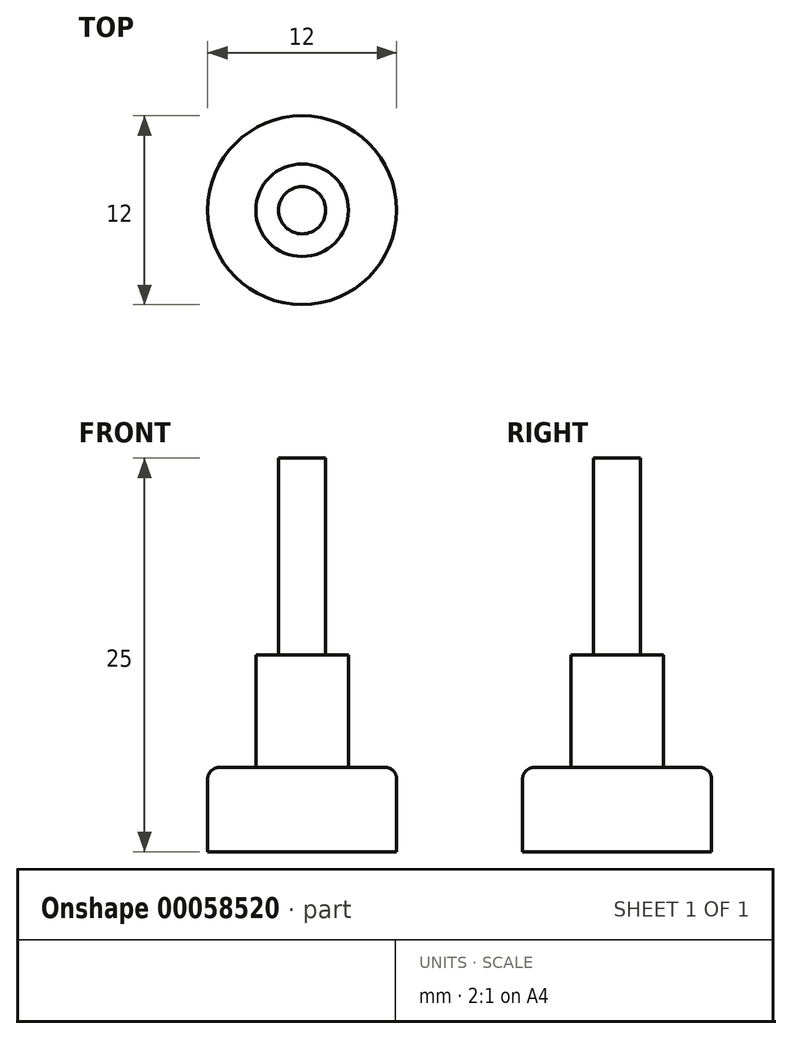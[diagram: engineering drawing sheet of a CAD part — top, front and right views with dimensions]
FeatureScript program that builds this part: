
annotation { "Feature Type Name" : "Feature", "Feature Type Description" : "" }
export const myFeature = defineFeature(function(context is Context, id is Id, definition is map)
    precondition{}
    {
        {
            var Q0;
            Q0=qCreatedBy(makeId("Top.planeOp"),FACE);
            var sketch = newSketch(context, id + "F0", { "sketchPlane" : qUnion([Q0])});
            skCircle(sketch, "E0", {"center": v(0, 0) * mm, "radius": 6 * mm});
            skCircle(sketch, "E1", {"center": v(0, 0) * mm, "radius": 2.94 * mm});
            skCircle(sketch, "E2", {"center": v(0, 0) * mm, "radius": 1.5 * mm});
            skSolve(sketch);
        }
        {
            var Q0;
            Q0=makeQuery(id+"F0.imprint","IMPRINT",FACE,{"disambiguationData":[TD([[makeQuery(id+"F0.imprint","IMPRINT",EDGE,{"derivedFrom":sQuery(id+"F0.wireOp",EDGE,"E2")}),1.0]])]});
            extrude(context, id + "F1", {"entities" : qUnion([Q0]), "depth" : 25 * mm});
        }
        {
            var Q0;
            Q0=makeQuery(id+"F0.imprint","IMPRINT",FACE,{"disambiguationData":[TD([[makeQuery(id+"F0.imprint","IMPRINT",EDGE,{"derivedFrom":sQuery(id+"F0.wireOp",EDGE,"E1")}),1.0]])]});
            extrude(context, id + "F2", {"entities" : qUnion([Q0]), "operationType" : NewBodyOperationType.ADD, "depth" : 12.5 * mm});
        }
        {
            var Q0;
            Q0=makeQuery(id+"F0.imprint","IMPRINT",FACE,{"disambiguationData":[TD([[makeQuery(id+"F0.imprint","IMPRINT",EDGE,{"derivedFrom":sQuery(id+"F0.wireOp",EDGE,"E0")}),1.0]])]});
            extrude(context, id + "F3", {"entities" : qUnion([Q0]), "operationType" : NewBodyOperationType.ADD, "depth" : 5.37 * mm});
        }
        {
            var Q0;
            Q0=makeQuery(id+"F3.opExtrude","CAP_EDGE",EDGE,{"disambiguationData":[OSD([sQuery(id+"F0.wireOp",EDGE,"E0")])],"isStart":false});
            fillet(context, id + "F4", {"entities" : qUnion([Q0]), "radius" : .75 * mm, "tangentPropagation" : true, "allowEdgeOverflow" : false});
        }
    });
